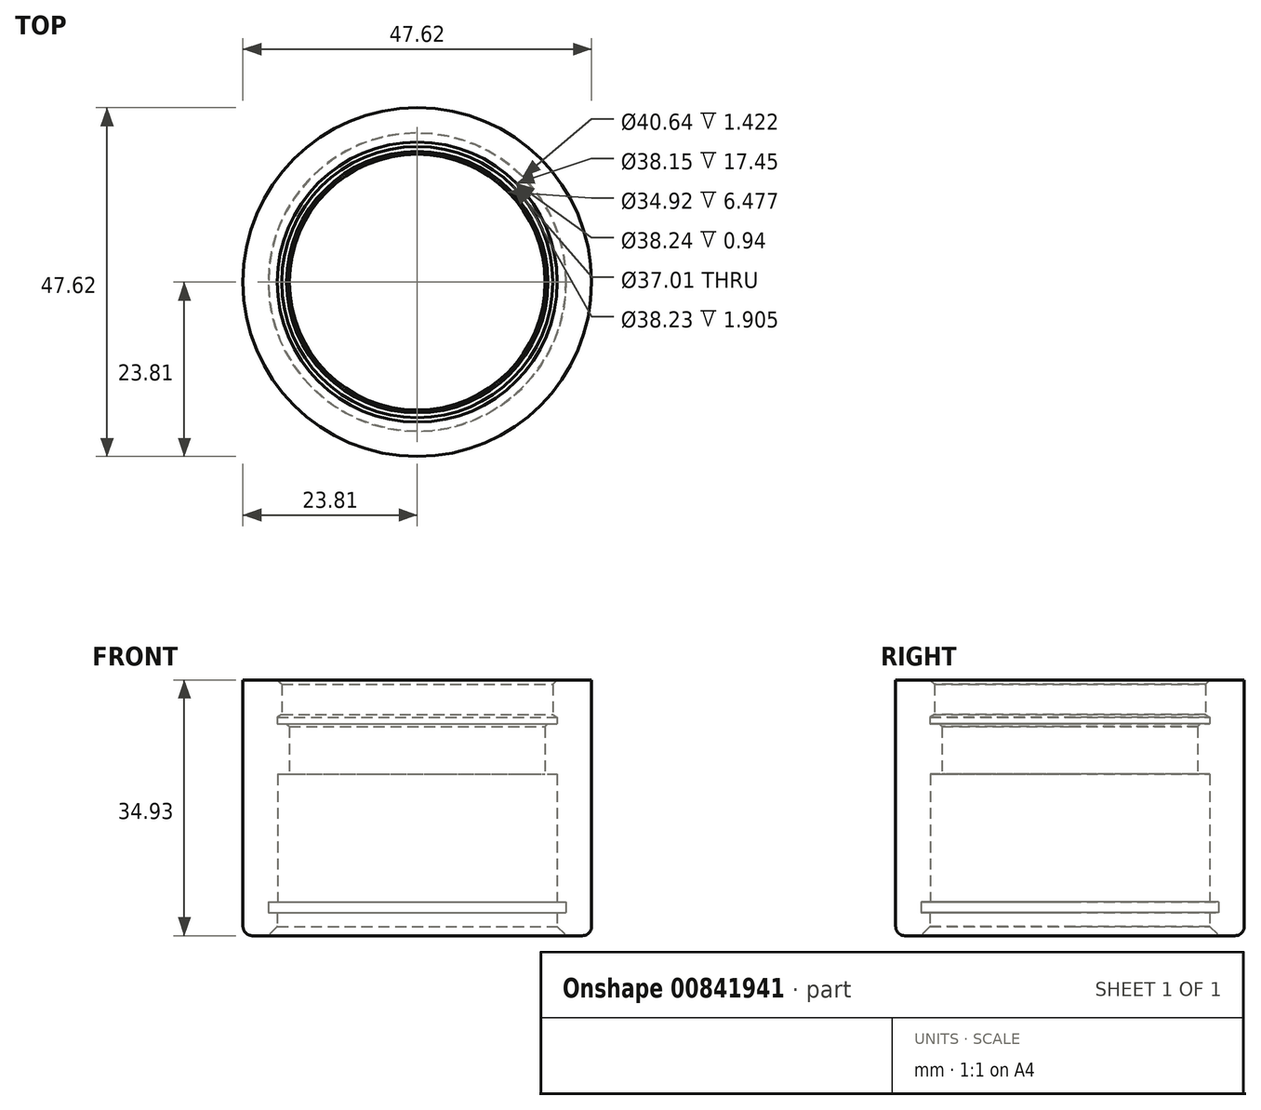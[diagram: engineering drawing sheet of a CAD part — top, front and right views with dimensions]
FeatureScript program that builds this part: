
annotation { "Feature Type Name" : "Feature", "Feature Type Description" : "" }
export const myFeature = defineFeature(function(context is Context, id is Id, definition is map)
    precondition{}
    {
        {
            var Q0;
            Q0=qCreatedBy(makeId("Front.planeOp"),FACE);
            var sketch = newSketch(context, id + "F0", { "sketchPlane" : qUnion([Q0])});
            skLineSegment(sketch, "E0", {"start": v(-23.81, 34.93) * mm, "end": v(-23.81, 0) * mm});
            skLineSegment(sketch, "E1", {"start": v(-23.81, 34.93) * mm, "end": v(-19.12, 34.93) * mm});
            skLineSegment(sketch, "E2", {"start": v(-18.5, 34.3) * mm, "end": v(-18.5, 30.2) * mm});
            skLineSegment(sketch, "E3", {"start": v(-19.12, 28.9) * mm, "end": v(-17.84, 28.9) * mm});
            skLineSegment(sketch, "E4", {"start": v(-17.46, 28.52) * mm, "end": v(-17.46, 22.05) * mm});
            skLineSegment(sketch, "E5", {"start": v(-17.46, 22.05) * mm, "end": v(-19.08, 22.05) * mm});
            skLineSegment(sketch, "E6", {"start": v(-19.08, 22.05) * mm, "end": v(-19.08, 4.6) * mm});
            skLineSegment(sketch, "E7", {"start": v(-19.08, 4.6) * mm, "end": v(-20.32, 4.6) * mm});
            skLineSegment(sketch, "E8", {"start": v(-20.32, 4.6) * mm, "end": v(-20.32, 3.18) * mm});
            skLineSegment(sketch, "E9", {"start": v(-20.32, 3.17) * mm, "end": v(-19.11, 3.17) * mm});
            skLineSegment(sketch, "E10", {"start": v(-19.11, 3.18) * mm, "end": v(-19.11, 1.27) * mm});
            skLineSegment(sketch, "E11", {"start": v(-19.11, 1.27) * mm, "end": v(-20.38, 0) * mm});
            skLineSegment(sketch, "E12", {"start": v(-20.38, 0) * mm, "end": v(-23.81, 0) * mm});
            skLineSegment(sketch, "E13", {"start": v(0, 0) * mm, "end": v(0, 24.7) * mm, "construction": true});
            skLineSegment(sketch, "E14", {"start": v(-19.12, 29.85) * mm, "end": v(-19.12, 28.9) * mm});
            skLineSegment(sketch, "E15", {"start": v(-19.12, 34.93) * mm, "end": v(-18.5, 34.3) * mm});
            skLineSegment(sketch, "E16", {"start": v(-19.12, 29.85) * mm, "end": v(-18.5, 30.2) * mm});
            skLineSegment(sketch, "E17", {"start": v(-17.84, 28.9) * mm, "end": v(-17.46, 28.52) * mm});
            skSolve(sketch);
        }
        {
            var Q0;
            Q0=qSketchRegion(id+"F0",true);
            var Q1;
            Q1=sQuery(id+"F0.wireOp",EDGE,"E13");
            revolve(context, id + "F1", {"surfaceOperationType" : NewSurfaceOperationType.NEW, "entities" : qUnion([Q0]), "axis" : qUnion([Q1]), "revolveType" : RevolveType.FULL});
        }
        {
            var Q0;
            Q0=makeQuery(id+"F1.opRevolve","SWEPT_FACE",FACE,{"disambiguationData":[OSD([sQuery(id+"F0.wireOp",EDGE,"E1")])]});
            var sketch = newSketch(context, id + "F2", { "sketchPlane" : qUnion([Q0])});
            skCircle(sketch, "E18.0", {"center": v(0, 0) * mm, "radius": 18.5 * mm});
            skSolve(sketch);
        }
        {
            var Q0;
            Q0=qCreatedBy(makeId("Front.planeOp"),FACE);
            var sketch = newSketch(context, id + "F3", { "sketchPlane" : qUnion([Q0])});
            skLineSegment(sketch, "E19", {"start": v(24.8, 35.79) * mm, "end": v(25.4, 35.44) * mm});
            skLineSegment(sketch, "E20", {"start": v(24.8, 35.79) * mm, "end": v(24.8, 34.93) * mm});
            skLineSegment(sketch, "E21", {"start": v(25.4, 35.28) * mm, "end": v(24.8, 34.93) * mm});
            skLineSegment(sketch, "E22", {"start": v(25.4, 35.28) * mm, "end": v(25.4, 35.44) * mm});
            skLineSegment(sketch, "E23", {"start": v(0, 0) * mm, "end": v(0, 41.3) * mm, "construction": true});
            skLineSegment(sketch, "E24", {"start": v(25.4, 35.36) * mm, "end": v(24.8, 35.36) * mm, "construction": true});
            skSolve(sketch);
        }
        {
            var Q0;
            Q0=makeQuery(id+"F1.opRevolve","SWEPT_EDGE",EDGE,{"disambiguationData":[OSD([sQuery(id+"F0.wireOp",EDGE,"E0"),sQuery(id+"F0.wireOp",EDGE,"E12")])]});
            fillet(context, id + "F4", {"entities" : qUnion([Q0]), "radius" : 1.27 * mm, "tangentPropagation" : true, "allowEdgeOverflow" : false});
        }
    });
